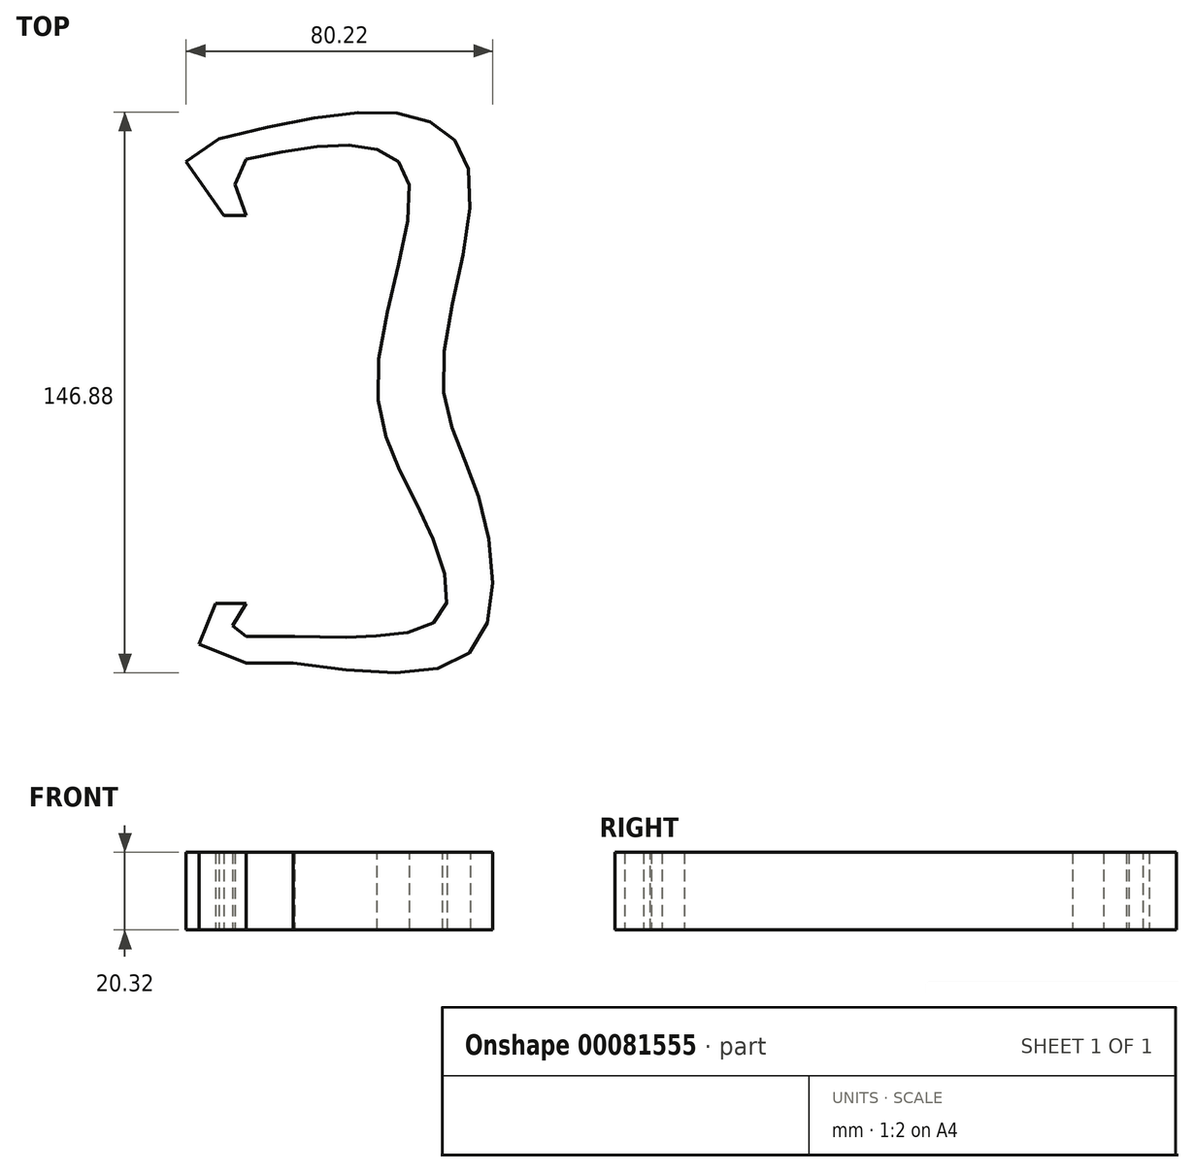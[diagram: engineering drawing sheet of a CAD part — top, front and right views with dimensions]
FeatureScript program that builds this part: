
annotation { "Feature Type Name" : "Feature", "Feature Type Description" : "" }
export const myFeature = defineFeature(function(context is Context, id is Id, definition is map)
    precondition{}
    {
        {
            var Q0;
            Q0=qCreatedBy(makeId("Top.planeOp"),FACE);
            var sketch = newSketch(context, id + "F0", { "sketchPlane" : qUnion([Q0])});
            skLineSegment(sketch, "E0", {"start": v(0, 41.5) * mm, "end": v(-5.8, 41.5) * mm});
            skLineSegment(sketch, "E1", {"start": v(-5.8, 41.5) * mm, "end": v(-15.64, 55.6) * mm});
            skLineSegment(sketch, "E2", {"start": v(-15.64, 55.6) * mm, "end": v(-7.03, 61.6) * mm});
            skFitSpline(sketch, "E3", {"points": [v(-7.03, 61.6) * mm, v(41.89, 67.95) * mm, v(58.49, 52.7) * mm, v(51.54, 0) * mm, v(61, -32.62) * mm, v(59.45, -72) * mm, v(12.35, -75.67) * mm], "startDerivative": vector(292.68, 71.23) * mm, "endDerivative": vector(-322.82, 44.63) * mm});
            skLineSegment(sketch, "E4", {"start": v(12.35, -75.67) * mm, "end": v(0, -75.67) * mm});
            skLineSegment(sketch, "E5", {"start": v(0, -75.67) * mm, "end": v(-12.27, -70.73) * mm});
            skLineSegment(sketch, "E6", {"start": v(-12.27, -70.73) * mm, "end": v(-8, -60.1) * mm});
            skLineSegment(sketch, "E7", {"start": v(-8, -60.1) * mm, "end": v(-3.65, -60.1) * mm});
            skPoint(sketch, "E8.endSnap0", {"position": v(-6.14, -73.2) * mm});
            skLineSegment(sketch, "E9", {"start": v(0, -68.74) * mm, "end": v(12.8, -68.74) * mm});
            skFitSpline(sketch, "E10", {"points": [v(12.8, -68.74) * mm, v(31.67, -68.74) * mm, v(51.54, -62.59) * mm, v(45.15, -35) * mm, v(34.4, 0) * mm, v(42.56, 50.29) * mm, v(30.57, 59.7) * mm, v(0, 56.28) * mm], "startDerivative": vector(147.7, -3.8) * mm, "endDerivative": vector(-219.76, -45.75) * mm});
            skLineSegment(sketch, "E11", {"start": v(0, 56.28) * mm, "end": v(-2.9, 49.68) * mm});
            skPoint(sketch, "E11.endSnap0", {"position": v(-2.9, 41.5) * mm});
            skLineSegment(sketch, "E12", {"start": v(-2.9, 49.68) * mm, "end": v(0, 41.5) * mm});
            skLineSegment(sketch, "E13", {"start": v(-3.65, -60.1) * mm, "end": v(0, -60.1) * mm});
            skLineSegment(sketch, "E14", {"start": v(0, -60.1) * mm, "end": v(-3.46, -65.94) * mm});
            skLineSegment(sketch, "E15", {"start": v(-3.46, -65.94) * mm, "end": v(0, -68.74) * mm});
            skPoint(sketch, "E8.end.orphan", {"position": v(-6.14, -66.27) * mm});
            skSolve(sketch);
        }
        {
            var Q0;
            Q0=makeQuery(id+"F0.imprint","IMPRINT",FACE,{"disambiguationData":[TD([[makeQuery(id+"F0.imprint","IMPRINT",EDGE,{"derivedFrom":sQuery(id+"F0.wireOp",EDGE,"E0")}),-1.0]])]});
            extrude(context, id + "F1", {"entities" : qUnion([Q0]), "depth" : 20.32 * mm});
        }
    });
